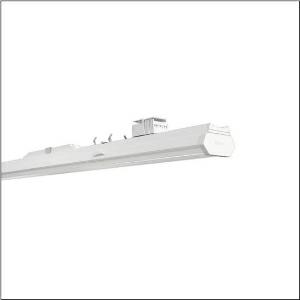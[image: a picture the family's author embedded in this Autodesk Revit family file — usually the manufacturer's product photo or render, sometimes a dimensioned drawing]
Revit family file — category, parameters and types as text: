
# Revit family: licross_r__21_protected_mo_52tp11mn4a5g_f46f
name_source: partatom
category: Lighting Fixtures
units: mm (PartAtom-declared; Revit-internal decimal feet)

## family parameters
Cut with Voids When Loaded = No
Host = Face
Light Source = No
Part Type = Normal
Room Calculation Point = No
Round Connector Dimension = Use Diameter
Shared = No

## types (1)
- --- (1 x LED, 10700 lm, 60.5 W, 4000K)
    Apparent Load = 61 VA
    CIE Flux Codes = 83 94 98 100 100
    Color Rendering = 80
    Color Temperature = 4000K
    Default Elevation = 1800 mm
    Description = Licross® 21 Protected MO, luminaire insert, of sheet steel, galvanised, coil coated, white, length: 1.500mm, width: 66mm, height: 67mm, LED rated luminous flux: 10.700lm, light colour: 840, control gear: ON/OFF Multilumen, with plug, 3-pole, with phase selection, mains connection: 220..240V, AC, 50/60Hz, rated input power: 61W, internal wiring halogen-free, primary light control with lens, of plastic, primary optical cover: cover, of PMMA, light emission: direct distribution, primary light characteristic: symmetric, protection rating (complete): IP64, insulation class (complete): insulation class I (protective earthing), certification: CE, ENEC, VDE, UKCA, protection symbol: D if used in an environment with conductive dust loads with corresponding accessories, impact resistance: IK06, permissible ambient temperature for indoor applications: -35..+45°C, corresponds to IFS (International Featured Standards) requirements for safety and quality in the food industry, reducing of maximum allowable ambient temperature of 5°C with ceiling mounting, LABS conformity tested according to VDMA 24364:2018-05, packaging unit: 1 piece
    Height = 92 mm
    Lamp = 1 x LED
    Lamp Light Flux = 10700 lm
    Lamp Power = 60.5 W
    Lamp count = 1
    Length = 1500 mm
    Luminous efficacy = 177 lm/W
    Manufacturer = Siteco
    ModVariant = No
    Model = 52TP11MN4A5G
    Mounting Place = Ceiling
    Mounting Type = Pendant
    Number of Poles = 1
    OnlyDefault = Yes
    Power Factor = 1
    Product Name = Licross® 21 Protected MO
    Product group = luminaire insert | ceiling pendant
    ProductGroupID = 902
    Protection Class = Protection class I
    Protection Degree = IP 64
    RLX_Detail_Level = 1
    RLX_Emergency_Light_Flux = 0 lm
    RLX_Emergency_Type = 0
    RLX_Emergency_Type_DB = No
    RlxData = <blob elided: 21913 chars, md5=01c8352a>
    Socket = socket
    Standby Power = 0 W
    System Light Flux = 10700 lm
    System Power = 61 W
    Type Comments = factory setting: luminous flux: 100 % | (A | C | E) | 140 mA
    Type Image = l_1256148.jpg
    URL = http://relux.com
    VarID = @adj_130495
    Voltage = 0 V
    Weight = 0.00 kg
    Width = 88 mm

## geometry (parser evidence)
native form markers: Blend x4, Sweep x12
no freeform markers — native parametric forms only
